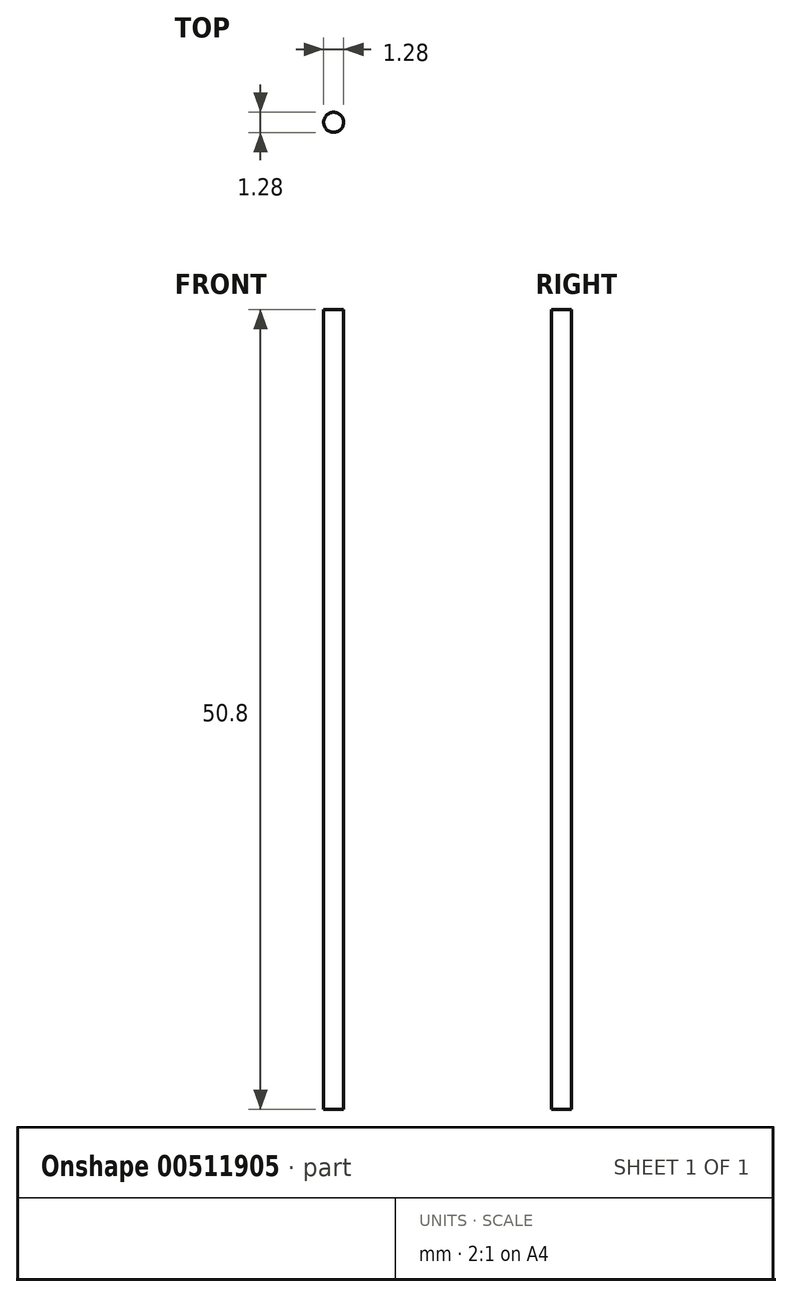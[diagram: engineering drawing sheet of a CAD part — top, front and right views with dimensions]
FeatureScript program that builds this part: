
annotation { "Feature Type Name" : "Feature", "Feature Type Description" : "" }
export const myFeature = defineFeature(function(context is Context, id is Id, definition is map)
    precondition{}
    {
        {
            var Q0;
            Q0=qCreatedBy(makeId("Top.planeOp"),FACE);
            var sketch = newSketch(context, id + "F0", { "sketchPlane" : qUnion([Q0])});
            skCircle(sketch, "E0", {"center": v(0, 0) * mm, "radius": 0.64 * mm});
            skSolve(sketch);
        }
        {
            var Q0;
            Q0 = qSketchRegion(id + "F0", true);
            extrude(context, id + "F1", {"entities" : qUnion([Q0]), "depth" : 50.8 * mm, "offsetDistance" : 25.4 * mm});
        }
    });
